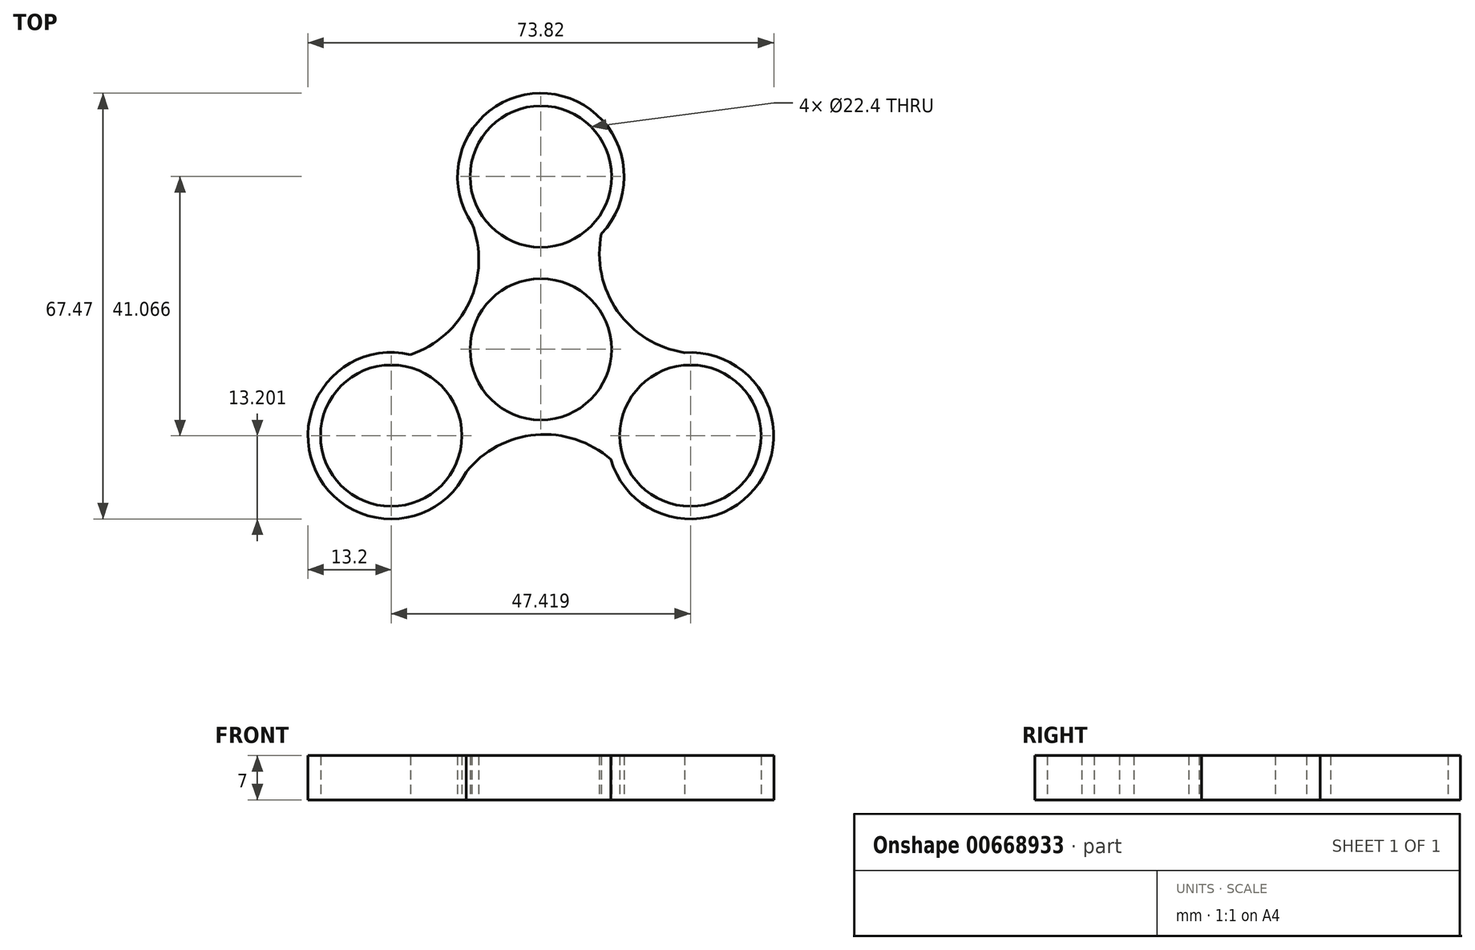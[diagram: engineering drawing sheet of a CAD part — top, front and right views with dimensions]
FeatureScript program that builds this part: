
annotation { "Feature Type Name" : "Feature", "Feature Type Description" : "" }
export const myFeature = defineFeature(function(context is Context, id is Id, definition is map)
    precondition{}
    {
        {
            var Q0;
            Q0=qCreatedBy(makeId("Top.planeOp"),FACE);
            var sketch = newSketch(context, id + "F0", { "sketchPlane" : qUnion([Q0])});
            skCircle(sketch, "E0", {"center": v(0, 0) * mm, "radius": 11.2 * mm});
            skCircle(sketch, "E1", {"center": v(0, 27.38) * mm, "radius": 11.2 * mm});
            skCircle(sketch, "E2", {"center": v(0, 27.38) * mm, "radius": 13.2 * mm});
            skCircle(sketch, "E3.1.0", {"center": v(-23.7, -13.69) * mm, "radius": 13.2 * mm});
            skCircle(sketch, "E3.2.0", {"center": v(23.7, -13.69) * mm, "radius": 13.2 * mm});
            skCircle(sketch, "E4.1.0", {"center": v(-23.7, -13.69) * mm, "radius": 11.2 * mm});
            skCircle(sketch, "E4.2.0", {"center": v(23.7, -13.69) * mm, "radius": 11.2 * mm});
            skArc(sketch, "E5", {"start": v(9.6, 18.31) * mm, "mid": v(12.14, 6.07) * mm, "end": v(22.76, -0.52) * mm});
            skArc(sketch, "E6.1.0", {"start": v(-20.66, -0.85) * mm, "mid": v(-11.33, 7.48) * mm, "end": v(-10.93, 19.97) * mm});
            skArc(sketch, "E6.2.0", {"start": v(11.06, -17.47) * mm, "mid": v(-0.81, -13.55) * mm, "end": v(-11.83, -19.45) * mm});
            skCircle(sketch, "E7", {"center": v(0, 0) * mm, "radius": 13.2 * mm});
            skSolve(sketch);
        }
        {
            var Q0;
            Q0=makeQuery(id+"F0.imprint","IMPRINT",FACE,{"disambiguationData":[TD([[makeQuery(id+"F0.imprint","IMPRINT",EDGE,{"derivedFrom":sQuery(id+"F0.wireOp",EDGE,"E1")}),-1.0]])]});
            var Q1;
            Q1=makeQuery(id+"F0.imprint","IMPRINT",FACE,{"disambiguationData":[TD([[makeQuery(id+"F0.imprint","IMPRINT",EDGE,{"derivedFrom":sQuery(id+"F0.wireOp",EDGE,"E4.1.0")}),-1.0]])]});
            var Q2;
            Q2=makeQuery(id+"F0.imprint","IMPRINT",FACE,{"disambiguationData":[TD([[makeQuery(id+"F0.imprint","IMPRINT",EDGE,{"derivedFrom":sQuery(id+"F0.wireOp",EDGE,"E4.2.0")}),-1.0]])]});
            var Q3;
            Q3=makeQuery(id+"F0.imprint","IMPRINT",FACE,{"disambiguationData":[TD([[makeQuery(id+"F0.imprint","IMPRINT",EDGE,{"derivedFrom":sQuery(id+"F0.wireOp",EDGE,"E0")}),-1.0]])]});
            var Q4;
            {var subQ0=sQuery(id+"F0.wireOp",EDGE,"E5");Q4=makeQuery(id+"F0.imprint","IMPRINT",FACE,{"disambiguationData":[TD([[makeQuery(id+"F0.imprint","IMPRINT",EDGE,{"derivedFrom":subQ0}),-1.0]])]});}
            extrude(context, id + "F1", {"entities" : qUnion([Q0, Q1, Q2, Q3, Q4]), "depth" : 7 * mm, "offsetDistance" : 25 * mm});
        }
    });
